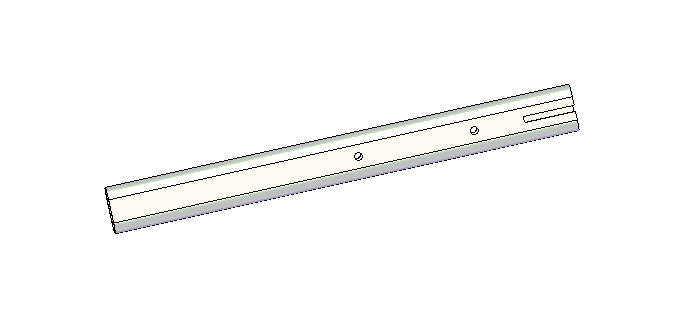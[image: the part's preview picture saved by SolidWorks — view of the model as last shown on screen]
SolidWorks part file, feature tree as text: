
SOLIDWORKS PART (.sldprt)
format: sldprt  version: not decoded by parser v0  size: 164,352 bytes
history: native  units: mm
features: plane x3, sketch x3, cut_extrude x2, extrude x1 + 1 further entry (+7 scaffold rows collapsed)
feature tree (17):
  scaffold x7  (default folders/planes/origin — collapsed)
  "Corps de surface"
  plane  "Face"
  plane  "Dessus"
  plane  "Droite"
  sketch  "Esquisse1"  dims[c1.D1=30.0mm c1.D3=7.5mm c1.D4=6.2mm c1.D5=6.2mm c2.D1=15.0mm c2.D2=15.0mm c2.D3=12.4mm]
  extrude  "Extrusion1"  Depth=300mm
  sketch  "Esquisse2"  dims[c1.D1=~3.522677mm c1.D2=6.0mm c1.D3=5.0mm c1.D4=5.0mm c2.D1=10.0mm c2.D2=65.0mm c3.D1=75.0mm]
  cut_extrude  "Enlèv. mat.-Extru.1"  [1 undecoded]
  sketch  "Esquisse3"  dims[D1=33.0mm D2=4.0mm]
  cut_extrude  "Enlèv. mat.-Extru.2"  Depth=10mm
decode coverage: 5 of 6 modeling features carry decoded parameters; 1 rows unclassified (native names shown)
note: ~ marks probable driven/reference dimensions
note: 1 parameter value undecoded
note: suppression state not decoded; provenance and decode notes live in map.json
